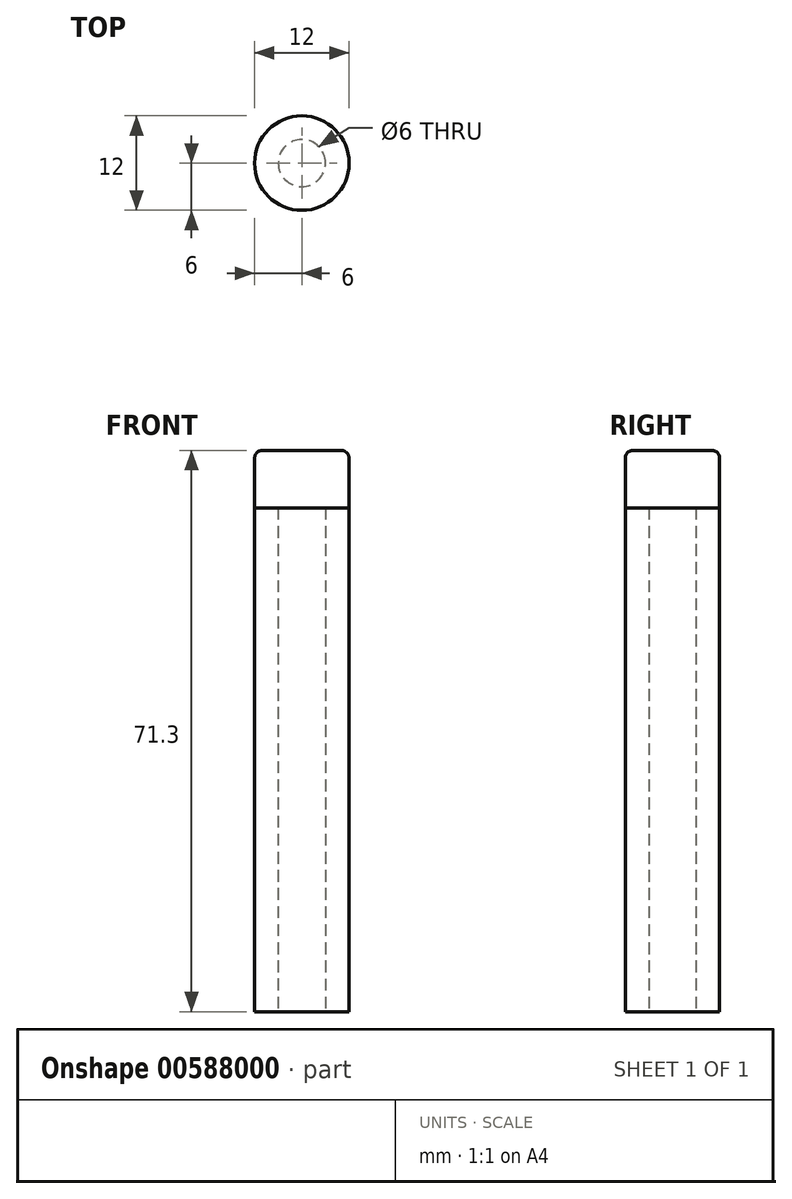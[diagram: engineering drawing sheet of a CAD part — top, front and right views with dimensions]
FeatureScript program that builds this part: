
annotation { "Feature Type Name" : "Feature", "Feature Type Description" : "" }
export const myFeature = defineFeature(function(context is Context, id is Id, definition is map)
    precondition{}
    {
        {
            var Q0;
            Q0=qCreatedBy(makeId("Top.planeOp"),FACE);
            var sketch = newSketch(context, id + "F0", { "sketchPlane" : qUnion([Q0])});
            skCircle(sketch, "E0", {"center": v(0, 0) * mm, "radius": 6 * mm});
            skCircle(sketch, "E1", {"center": v(0, 0) * mm, "radius": 3 * mm});
            skSolve(sketch);
        }
        {
            var Q0;
            Q0=makeQuery(id+"F0.imprint","IMPRINT",FACE,{"disambiguationData":[TD([[makeQuery(id+"F0.imprint","IMPRINT",EDGE,{"derivedFrom":sQuery(id+"F0.wireOp",EDGE,"E0")}),1.0]])]});
            extrude(context, id + "F1", {"entities" : qUnion([Q0]), "depth" : 64 * mm, "offsetDistance" : 25 * mm});
        }
        {
            var Q0;
            Q0=makeQuery(id+"F1.opExtrude","CAP_FACE",FACE,{"disambiguationData":[OSD([sQuery(id+"F0.wireOp",EDGE,"E0"),sQuery(id+"F0.wireOp",EDGE,"E1")])],"isStart":false});
            var sketch = newSketch(context, id + "F2", { "sketchPlane" : qUnion([Q0])});
            skCircle(sketch, "E2", {"center": v(0, 0) * mm, "radius": 6 * mm});
            skSolve(sketch);
        }
        {
            var Q0;
            Q0 = qSketchRegion(id + "F2", true);
            extrude(context, id + "F3", {"entities" : qUnion([Q0]), "depth" : 7.3 * mm, "offsetDistance" : 25 * mm});
        }
        {
            var Q0;
            Q0=makeQuery(id+"F3.opExtrude","CAP_EDGE",EDGE,{"disambiguationData":[OSD([sQuery(id+"F2.wireOp",EDGE,"E2")])],"isStart":false});
            fillet(context, id + "F4", {"entities" : qUnion([Q0]), "radius" : 1 * mm, "tangentPropagation" : true, "allowEdgeOverflow" : false});
        }
    });
